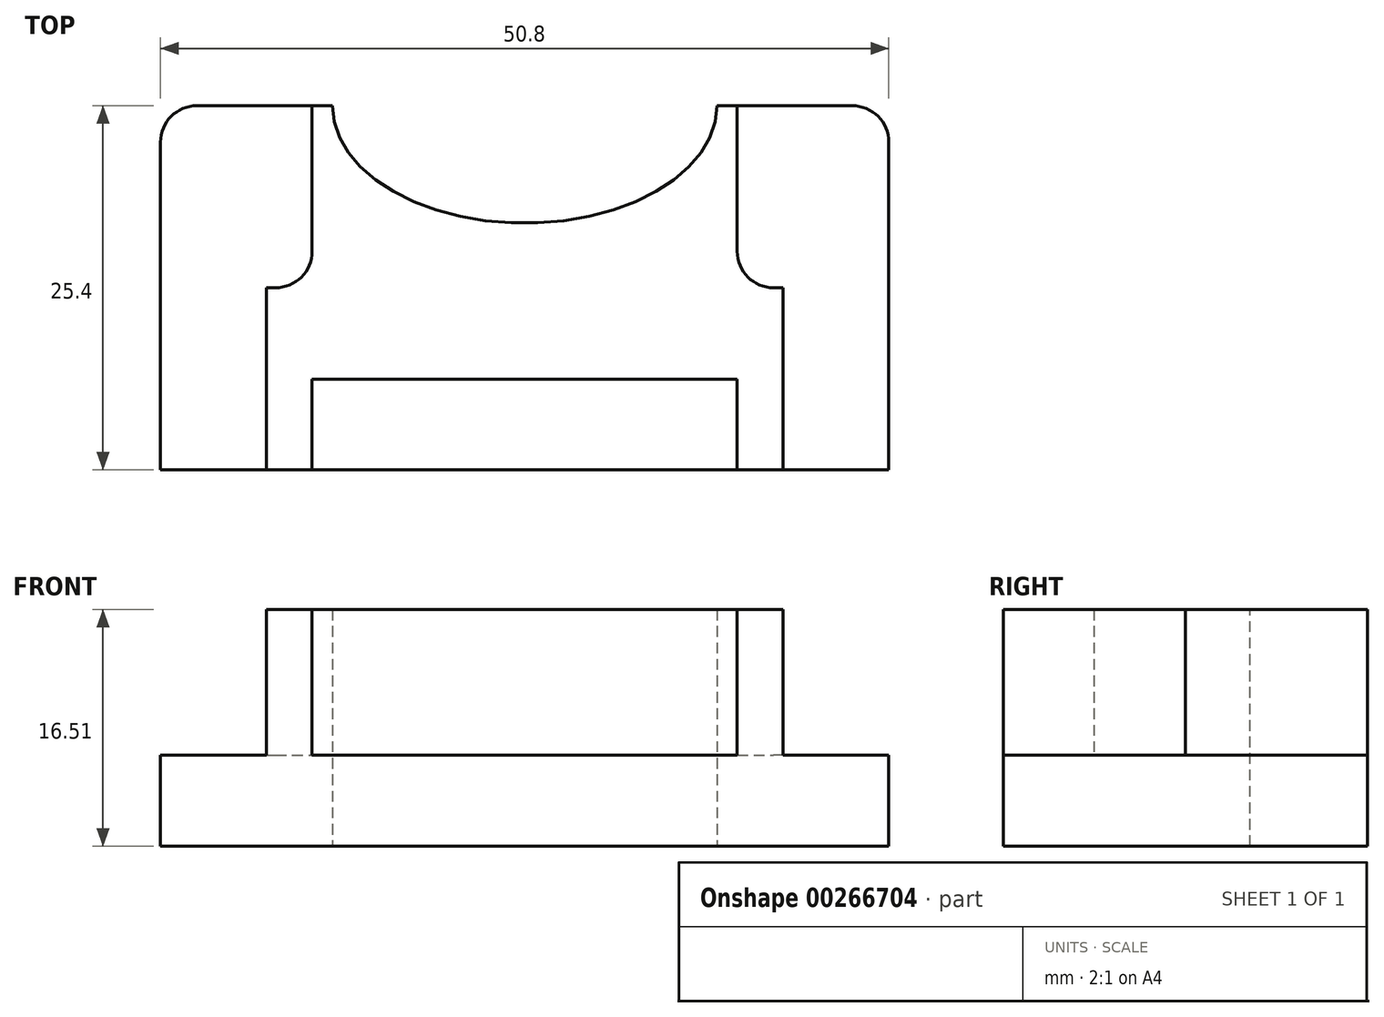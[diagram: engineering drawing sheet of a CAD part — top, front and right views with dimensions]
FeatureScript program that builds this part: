
annotation { "Feature Type Name" : "Feature", "Feature Type Description" : "" }
export const myFeature = defineFeature(function(context is Context, id is Id, definition is map)
    precondition{}
    {
        {
            var Q0;
            Q0=qCreatedBy(makeId("Top.planeOp"),FACE);
            var sketch = newSketch(context, id + "F0", { "sketchPlane" : qUnion([Q0])});
            skLineSegment(sketch, "E0.bottom", {"start": v(25.4, 12.7) * mm, "end": v(13.4, 12.7) * mm});
            skLineSegment(sketch, "E0.top", {"start": v(25.4, -12.7) * mm, "end": v(-25.4, -12.7) * mm});
            skLineSegment(sketch, "E0.left", {"start": v(25.4, 12.7) * mm, "end": v(25.4, -12.7) * mm});
            skLineSegment(sketch, "E0.right", {"start": v(-25.4, 12.7) * mm, "end": v(-25.4, -12.7) * mm});
            skPoint(sketch, "E0.middle", {"position": v(0, 0) * mm});
            skEllipticalArc(sketch, "E1", {});
            skLineSegment(sketch, "E2.trimOffspring", {"start": v(-13.4, 12.7) * mm, "end": v(-25.4, 12.7) * mm});
            const initialGuessF0  = {"E1": [0, 0.0127, 1, 0, 0.013407869264483454, 0.008189011532943496, 3.141592653589793, 0]};
            skSetInitialGuess(sketch, initialGuessF0);
            skSolve(sketch);
        }
        {
            var Q0;
            Q0=makeQuery(id+"F0.imprint","IMPRINT",FACE,{"disambiguationData":[TD([[makeQuery(id+"F0.imprint","IMPRINT",EDGE,{"derivedFrom":sQuery(id+"F0.wireOp",EDGE,"E0.bottom")}),1.0]])]});
            extrude(context, id + "F1", {"entities" : qUnion([Q0]), "depth" : 6.35 * mm});
        }
        {
            var Q0;
            Q0=makeQuery(id+"F1.opExtrude","CAP_FACE",FACE,{"disambiguationData":[OSD([sQuery(id+"F0.wireOp",EDGE,"E0.bottom"),sQuery(id+"F0.wireOp",EDGE,"E0.top"),sQuery(id+"F0.wireOp",EDGE,"E0.left"),sQuery(id+"F0.wireOp",EDGE,"E0.right"),sQuery(id+"F0.wireOp",EDGE,"E1"),sQuery(id+"F0.wireOp",EDGE,"E2.trimOffspring")])],"isStart":false});
            var sketch = newSketch(context, id + "F2", { "sketchPlane" : qUnion([Q0])});
            skLineSegment(sketch, "E3.bottom", {"start": v(-18.02, -12.7) * mm, "end": v(-14.83, -12.7) * mm});
            skLineSegment(sketch, "E3.left", {"start": v(-18.02, -12.7) * mm, "end": v(-18.02, -6.4) * mm});
            skLineSegment(sketch, "E3.right", {"start": v(-14.83, -12.7) * mm, "end": v(-14.83, -6.4) * mm});
            skLineSegment(sketch, "E4.bottom", {"start": v(-14.83, -6.4) * mm, "end": v(0, -6.4) * mm});
            skLineSegment(sketch, "E4.top", {"start": v(-18.02, 0) * mm, "end": v(-14.83, 0) * mm});
            skLineSegment(sketch, "E4.left", {"start": v(-18.02, -6.4) * mm, "end": v(-18.02, 0) * mm});
            skLineSegment(sketch, "E5.top", {"start": v(-13.4, 12.7) * mm, "end": v(-14.83, 12.7) * mm});
            skLineSegment(sketch, "E5.right", {"start": v(-14.83, 0) * mm, "end": v(-14.83, 12.7) * mm});
            skLineSegment(sketch, "E6", {"start": v(-14.83, 12.7) * mm, "end": v(-13.4, 12.7) * mm});
            skEllipticalArc(sketch, "E7", {});
            skLineSegment(sketch, "E8.MirrorCS", {"start": v(14.83, -6.4) * mm, "end": v(0, -6.4) * mm});
            skLineSegment(sketch, "E9.MirrorCS", {"start": v(14.83, -12.7) * mm, "end": v(14.83, -6.4) * mm});
            skLineSegment(sketch, "E10.MirrorCS", {"start": v(18.02, -6.4) * mm, "end": v(18.02, 0) * mm});
            skLineSegment(sketch, "E11.MirrorCS", {"start": v(18.02, -12.7) * mm, "end": v(18.02, -6.4) * mm});
            skLineSegment(sketch, "E12.MirrorCS", {"start": v(18.02, -12.7) * mm, "end": v(14.83, -12.7) * mm});
            skLineSegment(sketch, "E13.MirrorCS", {"start": v(14.83, 0) * mm, "end": v(14.83, 12.7) * mm});
            skLineSegment(sketch, "E14.MirrorCS", {"start": v(14.83, 12.7) * mm, "end": v(13.4, 12.7) * mm});
            skEllipticalArc(sketch, "E15.MirrorCS", {});
            skLineSegment(sketch, "E16.MirrorCS", {"start": v(18.02, 0) * mm, "end": v(14.83, 0) * mm});
            const initialGuessF2  = {"E7": [0, 0.0127, -1, 0, 0.013407869264483455, 0.008160824702068204, 0, 1.5707963267948966], "E15.MirrorCS": [0, 0.0127, 1, 0, 0.013407869264483455, 0.008160824702068204, 4.71238898038469, 0]};
            skSetInitialGuess(sketch, initialGuessF2);
            skSolve(sketch);
        }
        {
            var Q0;
            Q0=makeQuery(id+"F2.imprint","IMPRINT",FACE,{"disambiguationData":[TD([[makeQuery(id+"F2.imprint","IMPRINT",EDGE,{"derivedFrom":sQuery(id+"F2.wireOp",EDGE,"E3.bottom")}),-1.0]])]});
            extrude(context, id + "F3", {"entities" : qUnion([Q0]), "operationType" : NewBodyOperationType.ADD, "depth" : 10.16 * mm});
        }
        {
            var Q0;
            Q0=makeQuery(id+"F3.opExtrude","SWEPT_EDGE",EDGE,{"disambiguationData":[OSD([sQuery(id+"F2.wireOp",EDGE,"E13.MirrorCS"),sQuery(id+"F2.wireOp",EDGE,"E16.MirrorCS")])]});
            var Q1;
            Q1=makeQuery(id+"F3.opExtrude","SWEPT_EDGE",EDGE,{"disambiguationData":[OSD([sQuery(id+"F2.wireOp",EDGE,"E4.top"),sQuery(id+"F2.wireOp",EDGE,"E5.right")])]});
            var Q2;
            Q2=makeQuery(id+"F1.opExtrude","SWEPT_EDGE",EDGE,{"disambiguationData":[OSD([sQuery(id+"F0.wireOp",EDGE,"E0.bottom"),sQuery(id+"F0.wireOp",EDGE,"E0.left")])]});
            var Q3;
            Q3=makeQuery(id+"F1.opExtrude","SWEPT_EDGE",EDGE,{"disambiguationData":[OSD([sQuery(id+"F0.wireOp",EDGE,"E0.right"),sQuery(id+"F0.wireOp",EDGE,"E2.trimOffspring")])]});
            fillet(context, id + "F4", {"entities" : qUnion([Q0, Q1, Q2, Q3]), "radius" : 2.54 * mm, "tangentPropagation" : true, "allowEdgeOverflow" : false});
        }
    });
